# Revit family: Stay Wall Mounted_
name_source: partatom
category: Casework
revit_build: Autodesk Revit Architecture 2012 (Build: 20110916_2132(x64)
units: mm (PartAtom-declared; Revit-internal decimal feet)

## types (12) — shared parameters
Manufacturer = Korpinen Oy
URL = http://www.korpinen.com
zero-valued in all types: Height, Width

## per-type parameters (varying)
| type | Adjustable Height | Depth | Model | Type |
| Stay 10101 | No | 0 mm  [stored 0 ft] | 10101 Stay 1 - Support Rail | Stay : 10101 |
| Stay 10101 K | No | 0 mm  [stored 0 ft] | 10101 K Stay 1 - Support Rail | Stay : 10101 K |
| Stay 10101 P | No | 0 mm  [stored 0 ft] | 10101 P Stay 1 - Support Rail | Stay : 10101 P |
| Stay 10102 | No | 0 mm  [stored 0 ft] | 10102 Stay 2 - Support Rail | Stay : 10102 |
| Stay 10102 K | No | 0 mm  [stored 0 ft] | 10102 K Stay 2 - Support Rail | Stay : 10102  K |
| Stay 10102 P | No | 0 mm  [stored 0 ft] | 10102 P Stay 2 - Support Rail | Stay : 10102  P |
| Stay 10103 | No | 0 mm  [stored 0 ft] | 10103 Stay 3 - Support Rail | Stay : 10103 |
| Stay 10103 K | No | 0 mm  [stored 0 ft] | 10103 K Stay 3 - Support Rail | Stay : 10103 K |
| Stay 10103 P | No | 0 mm  [stored 0 ft] | 10103 P Stay 3 - Support Rail | Stay : 10103 P |
| Stay 10113 | Yes | 23 mm  [stored 0.0754593 ft] | 10113  Stay 13 - Support Rail | Stay : 10113 |
| Stay 10113 K | Yes | 23 mm  [stored 0.0754593 ft] | 10113 K Stay 13 - Support Rail | Stay : 10113 K |
| Stay 10113 P | Yes | 23 mm  [stored 0.0754593 ft] | 10113 P Stay 13 - Support Rail | Stay : 10113 P |

note: [stored X ft] marks values corroborated as IEEE doubles in the binary element streams (Revit-internal decimal feet)

## geometry (parser evidence)
native form markers: Blend x2, Sweep x8
no freeform markers — native parametric forms only
